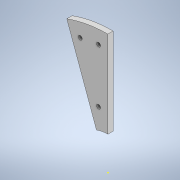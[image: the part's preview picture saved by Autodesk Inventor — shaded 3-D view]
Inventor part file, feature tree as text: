
AUTODESK INVENTOR PART (.ipt)
format: ipt  version: 2020.3 (Build 243373000, 373)  size: 154,112 bytes
history: native  units: mm
features: sketch x4, extrude x3, pattern_circular x1
ambient origin geometry x8: Origin, YZ Plane, XZ Plane, XY Plane, X Axis, Y Axis, Z Axis, Center Point
bodies: Solid1 (feature_tree)
feature tree (8):
  extrude  "Extrusion1"  Depth=25.0mm
  extrude  "Extrusion2"  Depth=4.0mm TaperAngle=0.0deg
  pattern_circular  "Circular Pattern1"  [2 undecoded]
  sketch  "Sketch3"  dims[d14=3.0mm]
  extrude  "Extrusion3"  Depth=80.0mm
  sketch  "Sketch1"  dims[d0=120.0deg d1=25.0mm]
  sketch  "Sketch2"  dims[d2=90.0mm d3=4.0mm d4=0.0mm]
  sketch  "Sketch4"  dims[d15=3.0mm d16=3.0mm d17=80.0mm d18=80.0mm d19=40.0mm d20=1.745329mm d21=0.872665mm d22=15.0deg d23=10.0mm d24=0.0mm d25=120.0mm d26=38.397244mm d29=3.490659mm d30=10.0mm d31=0.0mm]
note: 2 required parameter values undecoded (feature->parameter linkage not recoverable at this tier; creation-order binding heuristic only, values carry confidence <= 0.55)
